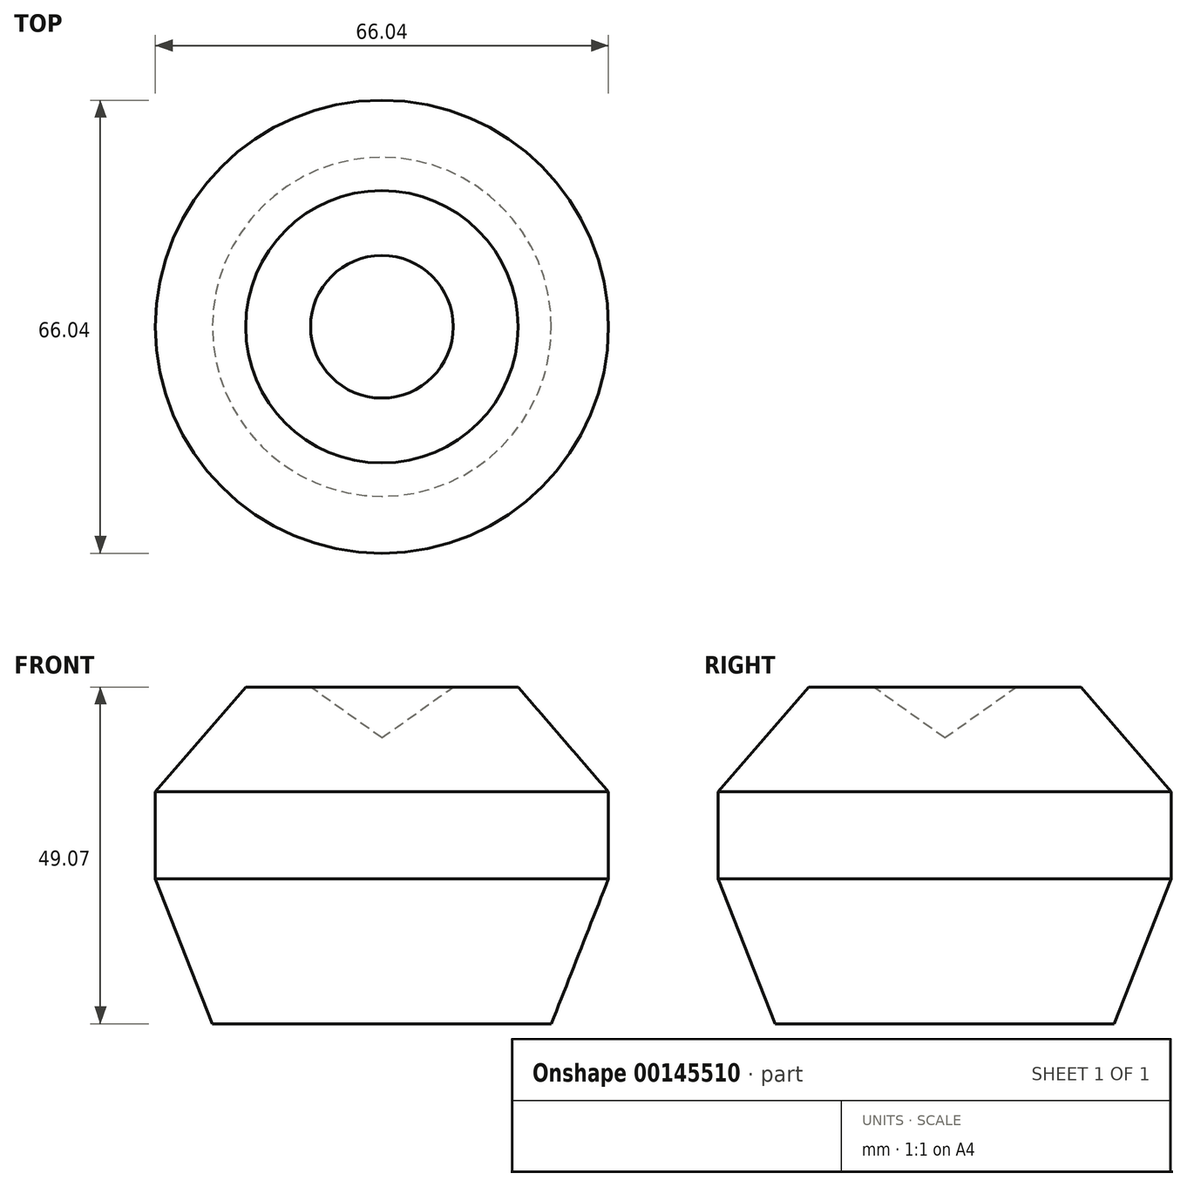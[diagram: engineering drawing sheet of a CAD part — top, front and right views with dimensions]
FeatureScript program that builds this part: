
annotation { "Feature Type Name" : "Feature", "Feature Type Description" : "" }
export const myFeature = defineFeature(function(context is Context, id is Id, definition is map)
    precondition{}
    {
        {
            var Q0;
            Q0=qCreatedBy(makeId("Right.planeOp"),FACE);
            var sketch = newSketch(context, id + "F0", { "sketchPlane" : qUnion([Q0])});
            skLineSegment(sketch, "E0", {"start": v(0, 0) * mm, "end": v(0, 50) * mm, "construction": true});
            skLineSegment(sketch, "E1", {"start": v(0, 0) * mm, "end": v(-25, 0) * mm});
            skSolve(sketch);
        }
        {
            var Q0;
            Q0=qCreatedBy(makeId("Right.planeOp"),FACE);
            var sketch = newSketch(context, id + "F1", { "sketchPlane" : qUnion([Q0])});
            skLineSegment(sketch, "E2", {"start": v(-24.7, 0) * mm, "end": v(-33.02, 21.13) * mm});
            skLineSegment(sketch, "E3", {"start": v(-33.02, 21.13) * mm, "end": v(-33.02, 33.83) * mm});
            skLineSegment(sketch, "E4", {"start": v(-33.02, 33.83) * mm, "end": v(-19.86, 49.07) * mm});
            skLineSegment(sketch, "E5", {"start": v(-19.86, 49.07) * mm, "end": v(-10.4, 49.07) * mm});
            skLineSegment(sketch, "E6", {"start": v(-10.4, 49.07) * mm, "end": v(0, 41.68) * mm});
            skLineSegment(sketch, "E7.MirrorCS", {"start": v(24.7, 0) * mm, "end": v(33.02, 21.13) * mm});
            skLineSegment(sketch, "E8.MirrorCS", {"start": v(33.02, 21.13) * mm, "end": v(33.02, 33.83) * mm});
            skLineSegment(sketch, "E9.MirrorCS", {"start": v(19.86, 49.07) * mm, "end": v(10.4, 49.07) * mm});
            skLineSegment(sketch, "E10.MirrorCS", {"start": v(10.4, 49.07) * mm, "end": v(0, 41.68) * mm});
            skLineSegment(sketch, "E11.MirrorCS", {"start": v(33.02, 33.83) * mm, "end": v(19.86, 49.07) * mm});
            skSolve(sketch);
        }
        {
            var Q0;
            Q0=sQuery(id+"F1.wireOp",EDGE,"E6");
            var Q1;
            Q1=sQuery(id+"F1.wireOp",EDGE,"E5");
            var Q2;
            Q2=sQuery(id+"F1.wireOp",EDGE,"E4");
            var Q3;
            Q3=sQuery(id+"F1.wireOp",EDGE,"E3");
            var Q4;
            Q4=sQuery(id+"F1.wireOp",EDGE,"E2");
            var Q5;
            Q5=sQuery(id+"F0.wireOp",EDGE,"E0");
            revolve(context, id + "F2", {"bodyType" : ToolBodyType.SURFACE, "surfaceEntities" : qUnion([Q0, Q1, Q2, Q3, Q4]), "axis" : qUnion([Q5]), "revolveType" : RevolveType.FULL});
        }
    });
